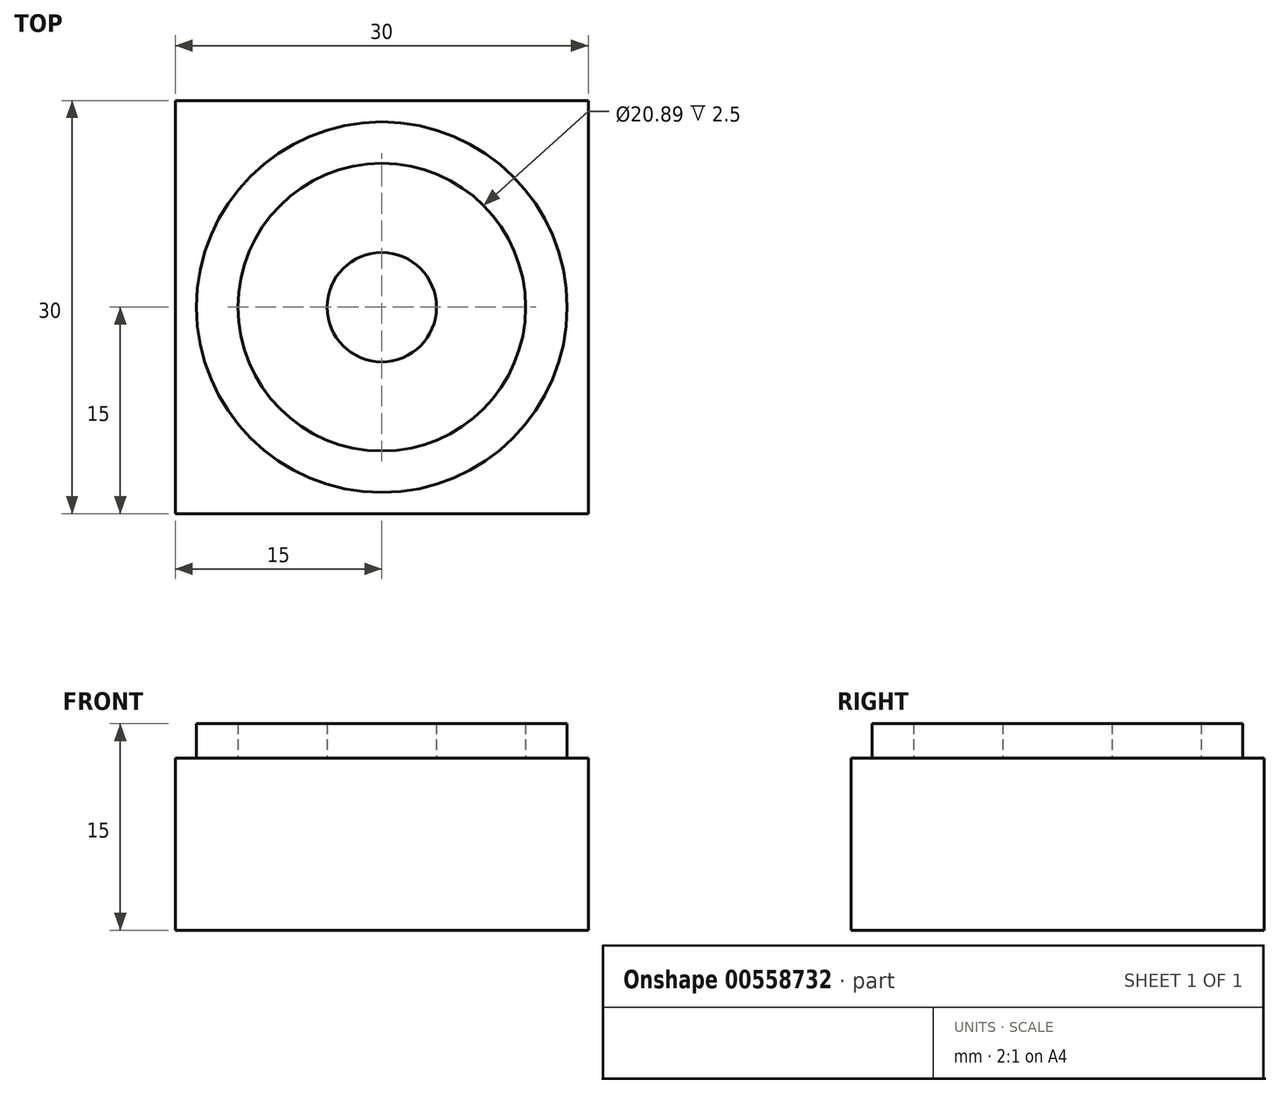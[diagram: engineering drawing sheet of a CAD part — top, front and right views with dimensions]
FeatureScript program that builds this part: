
annotation { "Feature Type Name" : "Feature", "Feature Type Description" : "" }
export const myFeature = defineFeature(function(context is Context, id is Id, definition is map)
    precondition{}
    {
        {
            var Q0;
            Q0=qCreatedBy(makeId("Top.planeOp"),FACE);
            var sketch = newSketch(context, id + "F0", { "sketchPlane" : qUnion([Q0])});
            skLineSegment(sketch, "E0.bottom", {"start": v(-15, 15) * mm, "end": v(15, 15) * mm});
            skLineSegment(sketch, "E0.top", {"start": v(-15, -15) * mm, "end": v(15, -15) * mm});
            skLineSegment(sketch, "E0.left", {"start": v(-15, 15) * mm, "end": v(-15, -15) * mm});
            skLineSegment(sketch, "E0.right", {"start": v(15, 15) * mm, "end": v(15, -15) * mm});
            skPoint(sketch, "E0.middle", {"position": v(0, 0) * mm});
            skSolve(sketch);
        }
        {
            var Q0;
            Q0 = qSketchRegion(id + "F0", true);
            extrude(context, id + "F1", {"entities" : qUnion([Q0]), "depth" : 12.5 * mm, "offsetDistance" : 25 * mm});
        }
        {
            var Q0;
            Q0=makeQuery(id+"F1.opExtrude","CAP_FACE",FACE,{"disambiguationData":[OSD([sQuery(id+"F0.wireOp",EDGE,"E0.bottom"),sQuery(id+"F0.wireOp",EDGE,"E0.top"),sQuery(id+"F0.wireOp",EDGE,"E0.left"),sQuery(id+"F0.wireOp",EDGE,"E0.right")])],"isStart":false});
            var sketch = newSketch(context, id + "F2", { "sketchPlane" : qUnion([Q0])});
            skCircle(sketch, "E1", {"center": v(0, 0) * mm, "radius": 3.97 * mm});
            skSolve(sketch);
        }
        {
            var Q0;
            Q0=makeQuery(id+"F2.imprint","IMPRINT",FACE,{"disambiguationData":[TD([[makeQuery(id+"F2.imprint","IMPRINT",EDGE,{"derivedFrom":sQuery(id+"F2.wireOp",EDGE,"E1")}),-1.0]])]});
            var sketch = newSketch(context, id + "F3", { "sketchPlane" : qUnion([Q0])});
            skCircle(sketch, "E2", {"center": v(0, 0) * mm, "radius": 13.46 * mm});
            skCircle(sketch, "E3", {"center": v(0, 0) * mm, "radius": 10.45 * mm});
            skSolve(sketch);
        }
        {
            var Q0;
            Q0 = qSketchRegion(id + "F3", true);
            extrude(context, id + "F4", {"entities" : qUnion([Q0]), "operationType" : NewBodyOperationType.ADD, "depth" : 2.5 * mm, "offsetDistance" : 25 * mm});
        }
        {
            var Q0;
            Q0 = qSketchRegion(id + "F2", true);
            extrude(context, id + "F5", {"entities" : qUnion([Q0]), "operationType" : NewBodyOperationType.ADD, "depth" : 2.5 * mm, "offsetDistance" : 25 * mm});
        }
    });
